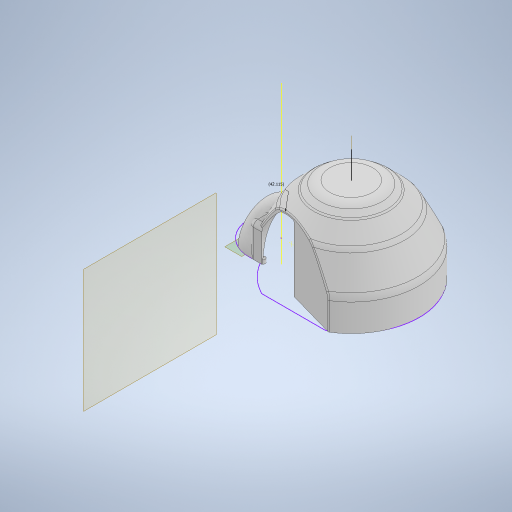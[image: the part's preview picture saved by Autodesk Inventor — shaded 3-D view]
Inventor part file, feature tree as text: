
AUTODESK INVENTOR PART (.ipt)
format: ipt  version: 2023 (Build 270158000, 158)  size: 613,376 bytes
history: native  units: in
note: dims shown in document units (in); Inventor stores cm internally (conversion verified against a paired STEP export)
features: sketch x9, extrude x9, other x7, fillet x5, plane x4, mirror x2
ambient origin geometry x8: Origin, YZ Plane, XZ Plane, XY Plane, X Axis, Y Axis, Z Axis, Center Point
bodies: Solid1 (feature_tree), BodySketch (feature_tree), Body (feature_tree)
feature tree (36):
  plane  "Work Plane2"
  other  "Base REF"
  plane  "Work Plane1"
  other  "Work Axis4"
  plane  "Work Plane4"
  sketch  "Sketch17"  dims[d105=1.6581in d108=210.0deg]
  other  "Work Axis5"
  other  "HeadRev"
  other  "AxisSketch"
  extrude  "SideCuts"  TaperAngle=210.0deg  [1 undecoded]
  plane  "Work Plane5"
  extrude  "Box"  Depth=0.7874in
  extrude  "SideWall"  Depth=2.6575in
  mirror  "Mirror2"
  fillet  "BoxFillet"  Radius=1.8701in
  extrude  "FrontCut"  Depth=3.3268in
  extrude  "HeadCut"  TaperAngle=360.0deg  [1 undecoded]
  fillet  "RounderFillets"  Radius=0.3937in
  fillet  "Fillet5"  Radius=0.6348in
  fillet  "Fillet7"  Radius=0.1181in
  fillet  "Fillet8"  Radius=6.8898in
  extrude  "MagnetHole"  Depth=0.7874in
  extrude  "Extrusion13"  Depth=0.7874in
  extrude  "Extrusion14"  Depth=0.3937in TaperAngle=0.0deg
  extrude  "Extrusion15"  Depth=0.1181in
  mirror  "Mirror3"
  other  "HeadSketch"
  other  "SideCutSketch"
  sketch  "Sketch20"  dims[d113=3.4449in d114=0.7874in]
  sketch  "Sketch21"  dims[d120=3.0512in d121=2.6575in d122=1.8701in]
  sketch  "Sketch22"  dims[d123=1.4764in d126=3.3268in]
  sketch  "Sketch23"  dims[d127=0.2756in d129=360.0deg d130=0.3937in d131=0.0in d132=0.6348in d133=0.0in d134=0.1181in d135=0.0in d136=6.8898in]
  sketch  "Sketch24"  dims[d137=0.7874in d138=0.7874in]
  sketch  "Sketch25"  dims[d139=0.2362in d140=0.7874in]
  sketch  "Sketch26"  dims[d141=0.0in d142=0.0in d143=0.3937in d144=0.0in]
  sketch  "Sketch27"  dims[d145=0.7874in d146=0.1181in d148=0.0787in d149=0.0787in d150=0.2362in d151=0.1969in d152=0.0in d153=0.1575in d154=0.1575in d155=0.0591in d156=0.0in d157=0.2362in d158=0.1575in d159=0.1969in d160=0.0in d161=0.1575in d162=0.0591in d163=0.0in d75=0.0197in d76=0.0344in d77=0.0197in d78=0.0344in d82=0.0344in d83=0.0344in d84=0.0197in d85=0.0344in d147=0.0in]
note: 2 required parameter values undecoded (feature->parameter linkage not recoverable at this tier; creation-order binding heuristic only, values carry confidence <= 0.55)
